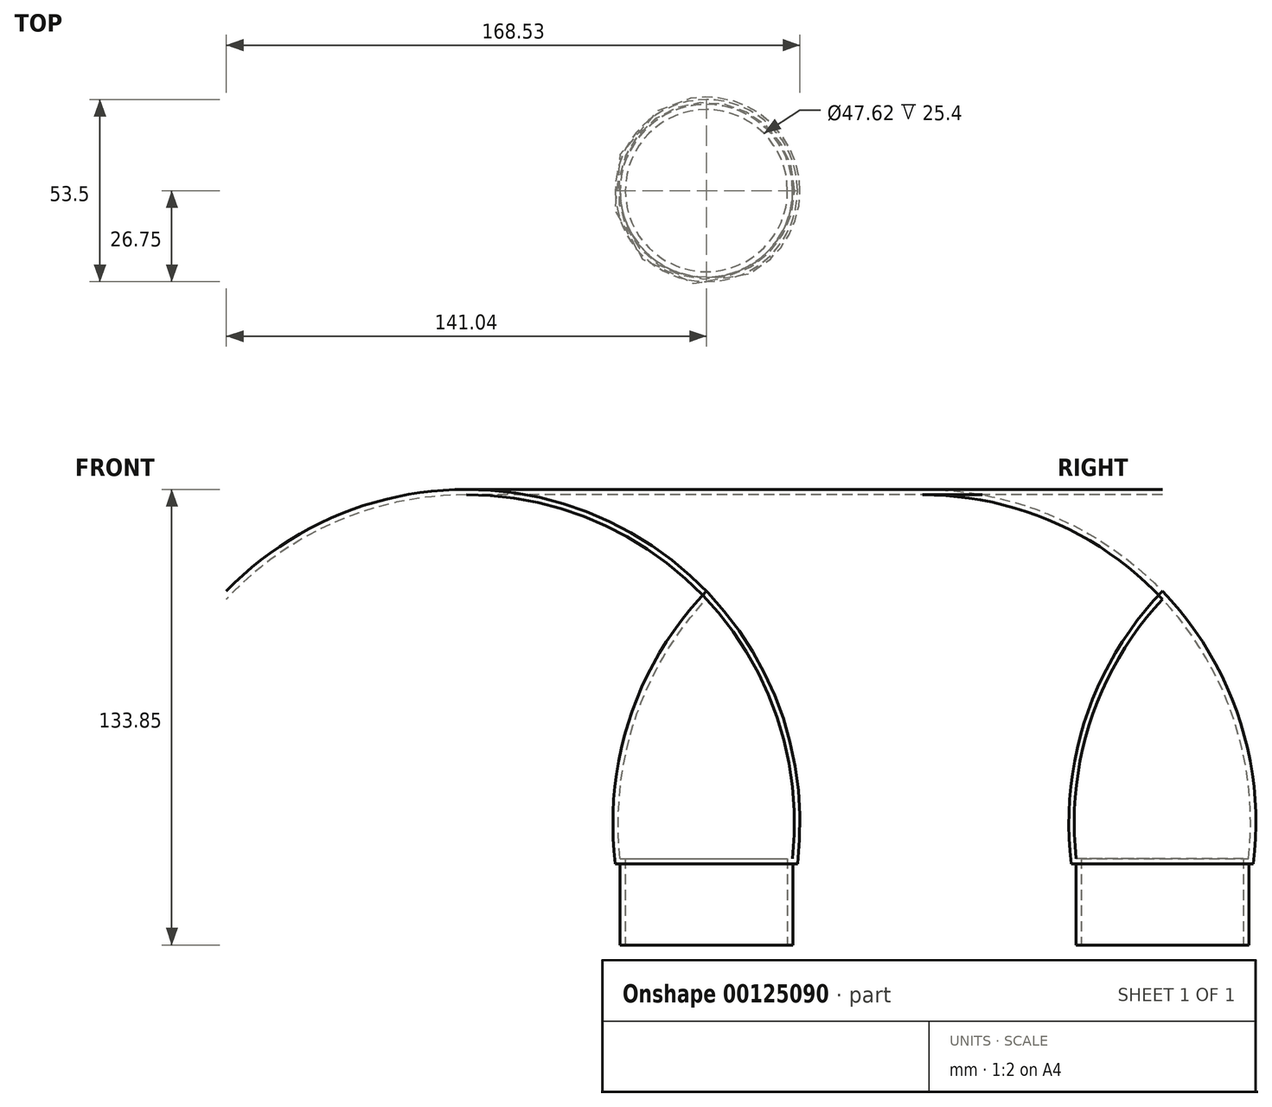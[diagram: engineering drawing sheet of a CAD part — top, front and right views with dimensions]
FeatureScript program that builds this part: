
annotation { "Feature Type Name" : "Feature", "Feature Type Description" : "" }
export const myFeature = defineFeature(function(context is Context, id is Id, definition is map)
    precondition{}
    {
        {
            var Q0;
            Q0=qCreatedBy(makeId("Front.planeOp"),FACE);
            var sketch = newSketch(context, id + "F0", { "sketchPlane" : qUnion([Q0])});
            skLineSegment(sketch, "E0", {"start": v(0, 0) * mm, "end": v(0, 101.6) * mm});
            skLineSegment(sketch, "E1", {"start": v(23.81, 0) * mm, "end": v(23.81, 25.4) * mm});
            skLineSegment(sketch, "E2", {"start": v(23.81, 25.4) * mm, "end": v(25.34, 25.4) * mm});
            skArc(sketch, "E3", {"start": v(25.34, 25.4) * mm, "mid": v(20.98, 66.26) * mm, "end": v(0, 101.6) * mm});
            skArc(sketch, "E4.0", {"start": v(26.75, 23.81) * mm, "mid": v(22.44, 66.89) * mm, "end": v(0, 103.9) * mm});
            skLineSegment(sketch, "E4.1", {"start": v(25.4, 23.81) * mm, "end": v(26.75, 23.81) * mm});
            skLineSegment(sketch, "E4.2", {"start": v(25.4, 0) * mm, "end": v(25.4, 23.81) * mm});
            skLineSegment(sketch, "E5", {"start": v(23.81, 0) * mm, "end": v(25.4, 0) * mm});
            skLineSegment(sketch, "E6", {"start": v(0, 101.6) * mm, "end": v(0, 103.9) * mm});
            skSolve(sketch);
        }
        {
            var Q0;
            Q0=makeQuery(id+"F0.imprint","IMPRINT",FACE,{"disambiguationData":[TD([[makeQuery(id+"F0.imprint","IMPRINT",EDGE,{"derivedFrom":sQuery(id+"F0.wireOp",EDGE,"E1")}),-1.0]])]});
            var Q1;
            Q1=sQuery(id+"F0.wireOp",EDGE,"E0");
            revolve(context, id + "F1", {"entities" : qUnion([Q0]), "axis" : qUnion([Q1]), "revolveType" : RevolveType.FULL});
        }
    });
